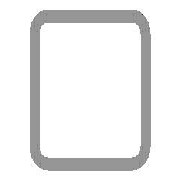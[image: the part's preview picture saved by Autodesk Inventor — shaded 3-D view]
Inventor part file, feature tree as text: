
AUTODESK INVENTOR PART (.ipt)
format: ipt  version: 2025 (Build 290162010, 162A)  size: 130,048 bytes
history: native  units: mm (DEFAULTED — no unit token found)
features: other x4, sketch x1, plane x1
ambient origin geometry x8: Origin, YZ Plane, XZ Plane, XY Plane, X Axis, Y Axis, Z Axis, Center Point
bodies: Solid1 (feature_tree), Body (feature_tree)
feature tree (6):
  parser-record x1  (decoder bookkeeping rows leaked as tree rows — omitted from the tree; the rows remain in map.json)
  other  "Driven Length"
  other  "Start Plane"
  other  "End Plane"
  sketch  "Sketch3"  dims[d3=2250.0mm d4=0.0mm d7=6.0mm d9=50.0mm d11=50.0mm d12=3.0mm d13=-0.0mm d14=2250.0mm d15=25.0mm d16=25.0mm d17=90.0deg d18=2250.0mm]
  plane  "Work Plane3"
